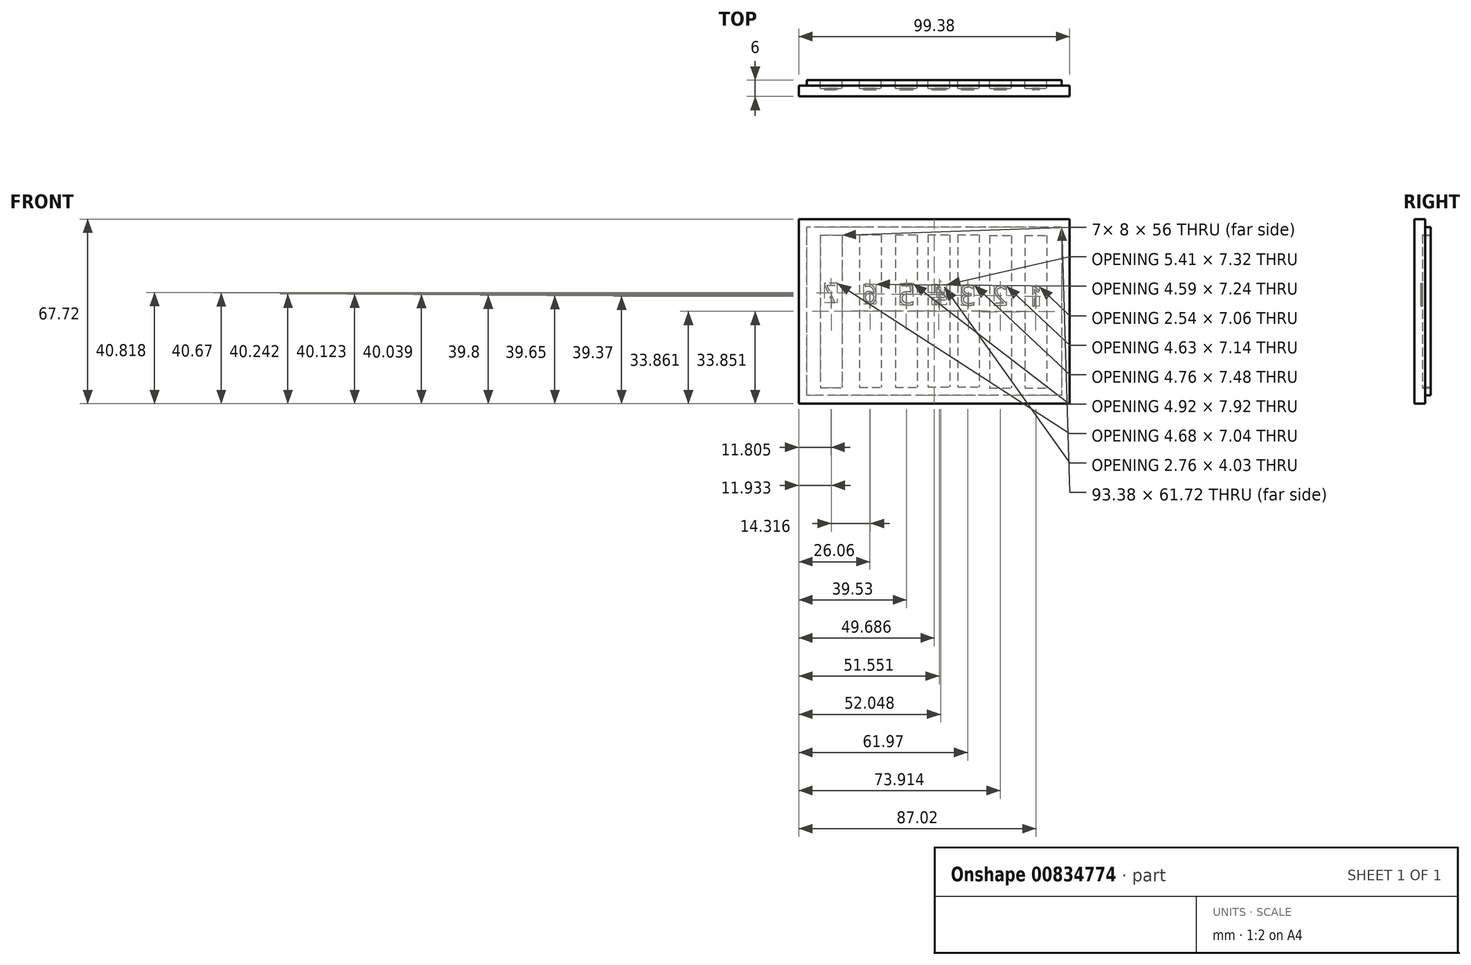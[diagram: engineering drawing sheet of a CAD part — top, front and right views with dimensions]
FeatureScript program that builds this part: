
annotation { "Feature Type Name" : "Feature", "Feature Type Description" : "" }
export const myFeature = defineFeature(function(context is Context, id is Id, definition is map)
    precondition{}
    {
        {
            var Q0;
            Q0=qCreatedBy(makeId("Front.planeOp"),FACE);
            var sketch = newSketch(context, id + "F0", { "sketchPlane" : qUnion([Q0])});
            skLineSegment(sketch, "E0.bottom", {"start": v(-44.74, 32.27) * mm, "end": v(-36.74, 32.27) * mm});
            skLineSegment(sketch, "E0.top", {"start": v(-44.74, -23.73) * mm, "end": v(-36.74, -23.73) * mm});
            skLineSegment(sketch, "E0.left", {"start": v(-44.74, 32.27) * mm, "end": v(-44.74, -23.73) * mm});
            skLineSegment(sketch, "E0.right", {"start": v(-36.74, 32.27) * mm, "end": v(-36.74, -23.73) * mm});
            skLineSegment(sketch, "E1.bottom", {"start": v(-30.42, 32.44) * mm, "end": v(-22.42, 32.44) * mm});
            skLineSegment(sketch, "E1.top", {"start": v(-30.42, -23.56) * mm, "end": v(-22.42, -23.56) * mm});
            skLineSegment(sketch, "E1.left", {"start": v(-30.42, 32.44) * mm, "end": v(-30.42, -23.56) * mm});
            skLineSegment(sketch, "E1.right", {"start": v(-22.42, 32.44) * mm, "end": v(-22.42, -23.56) * mm});
            skLineSegment(sketch, "E2.bottom", {"start": v(-17.22, 32.44) * mm, "end": v(-9.22, 32.44) * mm});
            skLineSegment(sketch, "E2.top", {"start": v(-17.22, -23.56) * mm, "end": v(-9.22, -23.56) * mm});
            skLineSegment(sketch, "E2.left", {"start": v(-17.22, 32.44) * mm, "end": v(-17.22, -23.56) * mm});
            skLineSegment(sketch, "E2.right", {"start": v(-9.22, 32.44) * mm, "end": v(-9.22, -23.56) * mm});
            skLineSegment(sketch, "E3.bottom", {"start": v(-5.3, 32.46) * mm, "end": v(2.7, 32.46) * mm});
            skLineSegment(sketch, "E3.top", {"start": v(-5.3, -23.54) * mm, "end": v(2.7, -23.54) * mm});
            skLineSegment(sketch, "E3.left", {"start": v(-5.3, 32.46) * mm, "end": v(-5.3, -23.54) * mm});
            skLineSegment(sketch, "E3.right", {"start": v(2.7, 32.46) * mm, "end": v(2.7, -23.54) * mm});
            skLineSegment(sketch, "E4.bottom", {"start": v(5.6, 32.46) * mm, "end": v(13.6, 32.46) * mm});
            skLineSegment(sketch, "E4.top", {"start": v(5.6, -23.54) * mm, "end": v(13.6, -23.54) * mm});
            skLineSegment(sketch, "E4.left", {"start": v(5.6, 32.46) * mm, "end": v(5.6, -23.54) * mm});
            skLineSegment(sketch, "E4.right", {"start": v(13.6, 32.46) * mm, "end": v(13.6, -23.54) * mm});
            skLineSegment(sketch, "E5.bottom", {"start": v(17.3, 32.13) * mm, "end": v(25.3, 32.13) * mm});
            skLineSegment(sketch, "E5.top", {"start": v(17.3, -23.87) * mm, "end": v(25.3, -23.87) * mm});
            skLineSegment(sketch, "E5.left", {"start": v(17.3, 32.13) * mm, "end": v(17.3, -23.87) * mm});
            skLineSegment(sketch, "E5.right", {"start": v(25.3, 32.13) * mm, "end": v(25.3, -23.87) * mm});
            skLineSegment(sketch, "E6.bottom", {"start": v(30.27, 32.19) * mm, "end": v(38.27, 32.19) * mm});
            skLineSegment(sketch, "E6.top", {"start": v(30.27, -23.81) * mm, "end": v(38.27, -23.81) * mm});
            skLineSegment(sketch, "E6.left", {"start": v(30.27, 32.19) * mm, "end": v(30.27, -23.81) * mm});
            skLineSegment(sketch, "E6.right", {"start": v(38.27, 32.19) * mm, "end": v(38.27, -23.81) * mm});
            skSolve(sketch);
        }
        {
            var Q0;
            Q0=qCreatedBy(makeId("Front.planeOp"),FACE);
            var sketch = newSketch(context, id + "F1", { "sketchPlane" : qUnion([Q0])});
            skLineSegment(sketch, "E7.bottom", {"start": v(-52.67, 38.14) * mm, "end": v(46.7, 38.14) * mm});
            skLineSegment(sketch, "E7.top", {"start": v(-52.67, -29.58) * mm, "end": v(46.7, -29.58) * mm});
            skLineSegment(sketch, "E7.left", {"start": v(-52.67, 38.14) * mm, "end": v(-52.67, -29.58) * mm});
            skLineSegment(sketch, "E7.right", {"start": v(46.7, 38.14) * mm, "end": v(46.7, -29.58) * mm});
            skSolve(sketch);
        }
        {
            var Q0;
            Q0=makeQuery(id+"F1.imprint","IMPRINT",FACE,{"disambiguationData":[TD([[makeQuery(id+"F1.imprint","IMPRINT",EDGE,{"derivedFrom":sQuery(id+"F1.wireOp",EDGE,"E7.bottom")}),-1.0]])]});
            extrude(context, id + "F2", {"entities" : qUnion([Q0]), "depth" : 6 * mm, "offsetDistance" : 25 * mm});
        }
        {
            var Q0;
            Q0 = qSketchRegion(id + "F0", true);
            extrude(context, id + "F3", {"entities" : qUnion([Q0]), "operationType" : NewBodyOperationType.REMOVE, "depth" : 3 * mm, "offsetDistance" : 25 * mm});
        }
        {
            var Q0;
            Q0=makeQuery(id+"F3.boolean.opBoolean","COPY",FACE,{"derivedFrom":makeQuery(id+"F3.opExtrude","CAP_FACE",FACE,{"disambiguationData":[OSD([sQuery(id+"F0.wireOp",EDGE,"E6.bottom"),sQuery(id+"F0.wireOp",EDGE,"E6.top"),sQuery(id+"F0.wireOp",EDGE,"E6.left"),sQuery(id+"F0.wireOp",EDGE,"E6.right")])],"isStart":false})});
            var sketch = newSketch(context, id + "F4", { "sketchPlane" : qUnion([Q0])});
            skText(sketch, "E8", { "text": "1", "fontName": "OpenSans-Regular.ttf"});
            skText(sketch, "E9", { "text": "2", "fontName": "OpenSans-Regular.ttf"});
            skText(sketch, "E10", { "text": "3", "fontName": "OpenSans-Regular.ttf"});
            skText(sketch, "E11", { "text": "4", "fontName": "OpenSans-Regular.ttf"});
            skText(sketch, "E12", { "text": "5", "fontName": "OpenSans-Regular.ttf"});
            skText(sketch, "E13", { "text": "6", "fontName": "OpenSans-Regular.ttf"});
            skText(sketch, "E14", { "text": "7", "fontName": "OpenSans-Regular.ttf"});
            const initialGuessF4  = {"E8": [-0.03653, 0.00626, 1, 0, 0.00712], "E9": [-0.02404, 0.0065, 1, 0, 0.0071], "E10": [-0.01215, 0.00658, 1, 0, 0.00734], "E11": [-0.0018, 0.0068, 1, 0, 0.00734], "E12": [0.00997, 0.00669, 1, 0, 0.00788], "E13": [0.02375, 0.00714, 1, 0, 0.0071], "E14": [0.03807, 0.00757, 1, 0, 0.0071]};
            skSetInitialGuess(sketch, initialGuessF4);
            skSolve(sketch);
        }
        {
            var Q0;
            Q0 = qSketchRegion(id + "F4", true);
            extrude(context, id + "F5", {"entities" : qUnion([Q0]), "operationType" : NewBodyOperationType.REMOVE, "oppositeDirection" : true, "depth" : 0.5 * mm, "offsetDistance" : 25 * mm});
        }
        {
            var Q0;
            Q0=makeQuery(id+"F2.opExtrude","CAP_FACE",FACE,{"disambiguationData":[OSD([sQuery(id+"F1.wireOp",EDGE,"E7.bottom"),sQuery(id+"F1.wireOp",EDGE,"E7.top"),sQuery(id+"F1.wireOp",EDGE,"E7.left"),sQuery(id+"F1.wireOp",EDGE,"E7.right")])],"isStart":true});
            var sketch = newSketch(context, id + "F6", { "sketchPlane" : qUnion([Q0])});
            skLineSegment(sketch, "E15.bottom", {"start": v(-46.7, 38.14) * mm, "end": v(52.67, 38.14) * mm});
            skLineSegment(sketch, "E15.top", {"start": v(-46.7, 35.14) * mm, "end": v(52.67, 35.14) * mm});
            skLineSegment(sketch, "E15.left", {"start": v(-46.7, 38.14) * mm, "end": v(-46.7, 35.14) * mm});
            skLineSegment(sketch, "E15.right", {"start": v(52.67, 38.14) * mm, "end": v(52.67, 35.14) * mm});
            skLineSegment(sketch, "E16.bottom", {"start": v(-46.7, -29.58) * mm, "end": v(52.67, -29.58) * mm});
            skLineSegment(sketch, "E16.top", {"start": v(-46.7, -26.58) * mm, "end": v(52.67, -26.58) * mm});
            skLineSegment(sketch, "E16.left", {"start": v(-46.7, -29.58) * mm, "end": v(-46.7, -26.58) * mm});
            skLineSegment(sketch, "E16.right", {"start": v(52.67, -29.58) * mm, "end": v(52.67, -26.58) * mm});
            skLineSegment(sketch, "E17.bottom", {"start": v(52.67, -29.58) * mm, "end": v(49.67, -29.58) * mm});
            skLineSegment(sketch, "E17.top", {"start": v(52.67, 38.14) * mm, "end": v(49.67, 38.14) * mm});
            skLineSegment(sketch, "E17.left", {"start": v(52.67, -29.58) * mm, "end": v(52.67, 38.14) * mm});
            skLineSegment(sketch, "E17.right", {"start": v(49.67, -29.58) * mm, "end": v(49.67, 38.14) * mm});
            skLineSegment(sketch, "E18.bottom", {"start": v(-46.7, 38.14) * mm, "end": v(-43.7, 38.14) * mm});
            skLineSegment(sketch, "E18.top", {"start": v(-46.7, -29.58) * mm, "end": v(-43.7, -29.58) * mm});
            skLineSegment(sketch, "E18.left", {"start": v(-46.7, 38.14) * mm, "end": v(-46.7, -29.58) * mm});
            skLineSegment(sketch, "E18.right", {"start": v(-43.7, 38.14) * mm, "end": v(-43.7, -29.58) * mm});
            skSolve(sketch);
        }
        {
            var Q0;
            Q0 = qSketchRegion(id + "F6", true);
            extrude(context, id + "F7", {"entities" : qUnion([Q0]), "operationType" : NewBodyOperationType.REMOVE, "oppositeDirection" : true, "depth" : 2 * mm, "offsetDistance" : 25 * mm});
        }
        {
            var Q0;
            Q0=makeQuery(id+"F2.opExtrude","SWEPT_BODY",BODY,{"disambiguationData":[OSD([sQuery(id+"F1.wireOp",EDGE,"E7.bottom"),sQuery(id+"F1.wireOp",EDGE,"E7.top"),sQuery(id+"F1.wireOp",EDGE,"E7.left"),sQuery(id+"F1.wireOp",EDGE,"E7.right")])]});
            transform(context, id + "F8", {"entities" : qUnion([Q0]), "transformType" : TransformType.TRANSLATION_3D, "dx" : 0 * mm, "dy" : 0 * mm, "dz" : 0 * mm, "makeCopy" : true});
        }
    });
